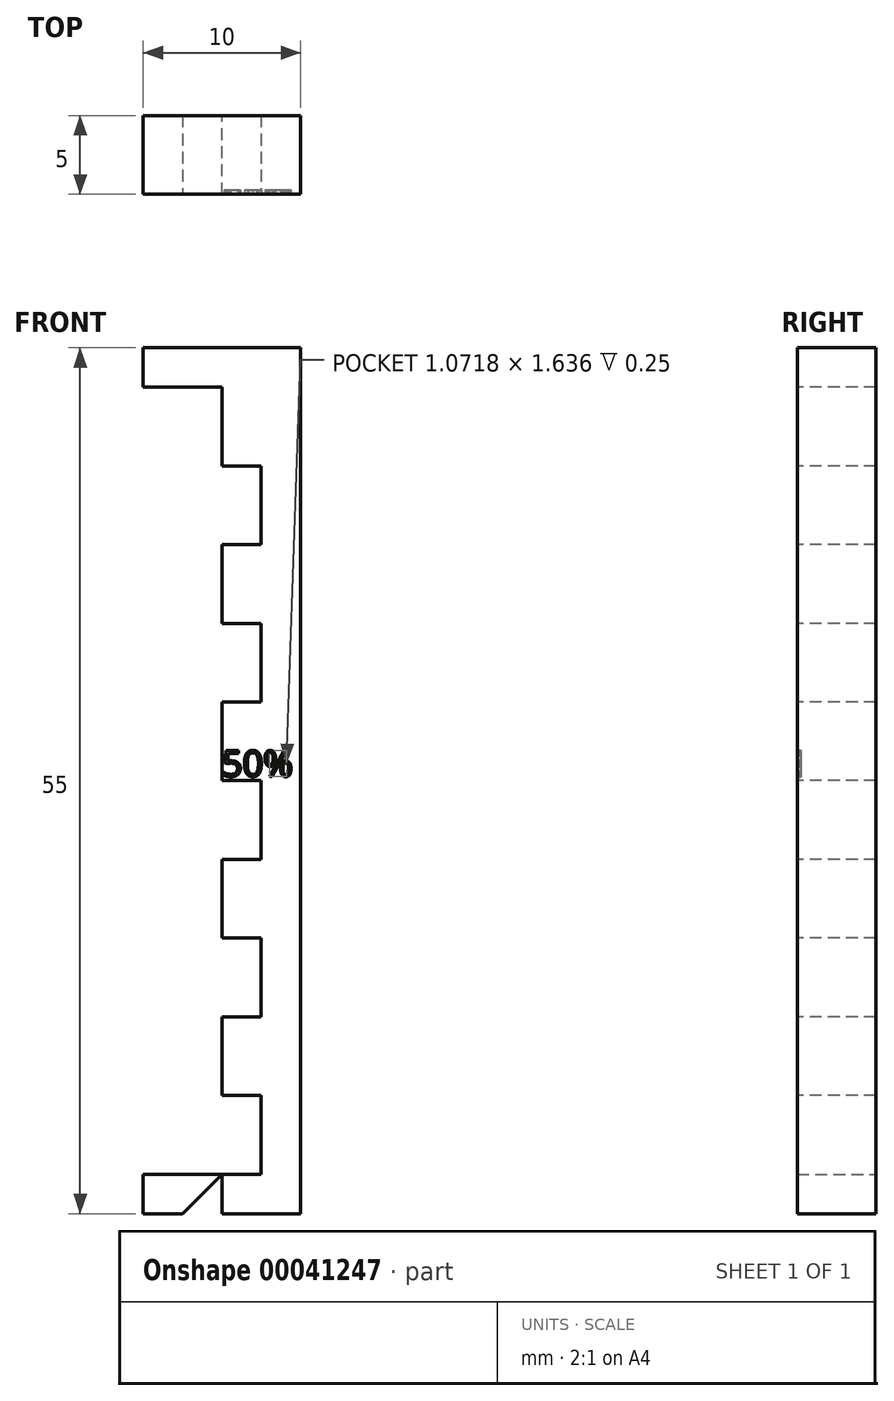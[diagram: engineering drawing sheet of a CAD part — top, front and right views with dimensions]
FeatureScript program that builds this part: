
annotation { "Feature Type Name" : "Feature", "Feature Type Description" : "" }
export const myFeature = defineFeature(function(context is Context, id is Id, definition is map)
    precondition{}
    {
        {
            var Q0;
            Q0=qCreatedBy(makeId("Front.planeOp"),FACE);
            var sketch = newSketch(context, id + "F0", { "sketchPlane" : qUnion([Q0])});
            skLineSegment(sketch, "E0.bottom", {"start": v(0, 10) * mm, "end": v(10, 10) * mm});
            skLineSegment(sketch, "E0.top", {"start": v(-10, -10) * mm, "end": v(10, -10) * mm});
            skLineSegment(sketch, "E0.left", {"start": v(-10, 0) * mm, "end": v(-10, -10) * mm});
            skLineSegment(sketch, "E0.right", {"start": v(10, 10) * mm, "end": v(10, -10) * mm});
            skLineSegment(sketch, "E1.top", {"start": v(-10, 0) * mm, "end": v(0, 0) * mm});
            skLineSegment(sketch, "E1.right", {"start": v(0, 10) * mm, "end": v(0, 0) * mm});
            skSolve(sketch);
        }
        {
            var Q0;
            Q0=makeQuery(id+"F0.imprint","IMPRINT",FACE,{"disambiguationData":[TD([[makeQuery(id+"F0.imprint","IMPRINT",EDGE,{"derivedFrom":sQuery(id+"F0.wireOp",EDGE,"E0.bottom")}),-1.0]])]});
            extrude(context, id + "F1", {"entities" : qUnion([Q0]), "oppositeDirection" : true, "depth" : 110 * mm});
        }
        {
            var Q0;
            Q0=makeQuery(id+"F1.opExtrude","CAP_FACE",FACE,{"disambiguationData":[OSD([sQuery(id+"F0.wireOp",EDGE,"E0.bottom"),sQuery(id+"F0.wireOp",EDGE,"E0.top"),sQuery(id+"F0.wireOp",EDGE,"E0.left"),sQuery(id+"F0.wireOp",EDGE,"E0.right"),sQuery(id+"F0.wireOp",EDGE,"E1.top"),sQuery(id+"F0.wireOp",EDGE,"E1.right")])],"isStart":true});
            var sketch = newSketch(context, id + "F2", { "sketchPlane" : qUnion([Q0])});
            skLineSegment(sketch, "E2.bottom", {"start": v(0, 10) * mm, "end": v(-10, 10) * mm});
            skLineSegment(sketch, "E2.top", {"start": v(0, 0) * mm, "end": v(-10, 0) * mm});
            skLineSegment(sketch, "E2.left", {"start": v(0, 10) * mm, "end": v(0, 0) * mm});
            skLineSegment(sketch, "E2.right", {"start": v(-10, 10) * mm, "end": v(-10, 0) * mm});
            skSolve(sketch);
        }
        {
            var Q0;
            Q0 = qSketchRegion(id + "F2", true);
            extrude(context, id + "F3", {"entities" : qUnion([Q0]), "oppositeDirection" : true, "depth" : 5 * mm});
        }
        {
            var Q0;
            Q0=makeQuery(id+"F3.opExtrude","CAP_EDGE",EDGE,{"disambiguationData":[OSD([sQuery(id+"F2.wireOp",EDGE,"E2.left")])],"isStart":true});
            chamfer(context, id + "F4", {"entities" : qUnion([Q0]), "width" : 5 * mm, "tangentPropagation" : true});
        }
        {
            var Q0;
            Q0=makeQuery(id+"F1.opExtrude","SWEPT_FACE",FACE,{"disambiguationData":[OSD([sQuery(id+"F0.wireOp",EDGE,"E0.bottom")])]});
            var sketch = newSketch(context, id + "F5", { "sketchPlane" : qUnion([Q0])});
            skLineSegment(sketch, "E3.bottom", {"start": v(-10, 115) * mm, "end": v(5, 115) * mm});
            skLineSegment(sketch, "E3.top", {"start": v(-10, 5) * mm, "end": v(5, 5) * mm});
            skLineSegment(sketch, "E3.left", {"start": v(-10, 115) * mm, "end": v(-10, 5) * mm});
            skLineSegment(sketch, "E3.right", {"start": v(5, 115) * mm, "end": v(5, 105) * mm});
            skLineSegment(sketch, "E4.top", {"start": v(0, 15) * mm, "end": v(5, 15) * mm});
            skLineSegment(sketch, "E4.left", {"start": v(0, 85) * mm, "end": v(0, 75) * mm});
            skLineSegment(sketch, "E5.bottom", {"start": v(0, 75) * mm, "end": v(5, 75) * mm});
            skLineSegment(sketch, "E5.top", {"start": v(0, 65) * mm, "end": v(5, 65) * mm});
            skLineSegment(sketch, "E6.bottom", {"start": v(0, 55) * mm, "end": v(5, 55) * mm});
            skLineSegment(sketch, "E6.top", {"start": v(0, 45) * mm, "end": v(5, 45) * mm});
            skLineSegment(sketch, "E7.bottom", {"start": v(0, 35) * mm, "end": v(5, 35) * mm});
            skLineSegment(sketch, "E7.top", {"start": v(0, 25) * mm, "end": v(5, 25) * mm});
            skLineSegment(sketch, "E8.trimOffspring", {"start": v(5, 15) * mm, "end": v(5, 5) * mm});
            skLineSegment(sketch, "E9.trimOffspring", {"start": v(0, 25) * mm, "end": v(0, 15) * mm});
            skLineSegment(sketch, "E10.trimOffspring", {"start": v(5, 35) * mm, "end": v(5, 25) * mm});
            skLineSegment(sketch, "E11.trimOffspring", {"start": v(0, 45) * mm, "end": v(0, 35) * mm});
            skLineSegment(sketch, "E12.trimOffspring", {"start": v(5, 55) * mm, "end": v(5, 45) * mm});
            skLineSegment(sketch, "E13.trimOffspring", {"start": v(5, 75) * mm, "end": v(5, 65) * mm});
            skLineSegment(sketch, "E14.trimOffspring", {"start": v(0, 65) * mm, "end": v(0, 55) * mm});
            skLineSegment(sketch, "E15", {"start": v(0, 85) * mm, "end": v(5, 85) * mm});
            skPoint(sketch, "E16.firstSnap0", {"position": v(5, 105) * mm});
            skLineSegment(sketch, "E16.bottom", {"start": v(0, 105) * mm, "end": v(5, 105) * mm});
            skLineSegment(sketch, "E16.top", {"start": v(0, 95) * mm, "end": v(5, 95) * mm});
            skLineSegment(sketch, "E16.left", {"start": v(0, 105) * mm, "end": v(0, 95) * mm});
            skLineSegment(sketch, "E17.trimOffspring", {"start": v(5, 95) * mm, "end": v(5, 85) * mm});
            skSolve(sketch);
        }
        {
            var Q0;
            Q0 = qSketchRegion(id + "F5", true);
            extrude(context, id + "F6", {"entities" : qUnion([Q0]), "operationType" : NewBodyOperationType.REMOVE, "oppositeDirection" : true, "depth" : 10 * mm});
        }
        {
            var Q0;
            Q0=makeQuery(id+"F1.opExtrude","SWEPT_FACE",FACE,{"disambiguationData":[OSD([sQuery(id+"F0.wireOp",EDGE,"E1.top")])]});
            var sketch = newSketch(context, id + "F7", { "sketchPlane" : qUnion([Q0])});
            skLineSegment(sketch, "E18.bottom", {"start": v(-10, 110) * mm, "end": v(5, 110) * mm});
            skLineSegment(sketch, "E18.top", {"start": v(-10, 105) * mm, "end": v(5, 105) * mm});
            skLineSegment(sketch, "E18.left", {"start": v(-10, 110) * mm, "end": v(-10, 105) * mm});
            skLineSegment(sketch, "E18.right", {"start": v(5, 110) * mm, "end": v(5, 105) * mm});
            skSolve(sketch);
        }
        {
            var Q0;
            Q0 = qSketchRegion(id + "F7", true);
            extrude(context, id + "F8", {"entities" : qUnion([Q0]), "operationType" : NewBodyOperationType.ADD, "depth" : 10 * mm});
        }
        {
            var Q0;
            Q0=makeQuery(id+"F8.boolean.opBoolean","MERGE",FACE,{"derivedFrom":[makeQuery(id+"F1.opExtrude","SWEPT_FACE",FACE,{"disambiguationData":[OSD([sQuery(id+"F0.wireOp",EDGE,"E0.bottom")])]}),makeQuery(id+"F8.opExtrude","CAP_FACE",FACE,{"disambiguationData":[OSD([sQuery(id+"F7.wireOp",EDGE,"E18.bottom"),sQuery(id+"F7.wireOp",EDGE,"E18.top"),sQuery(id+"F7.wireOp",EDGE,"E18.left"),sQuery(id+"F7.wireOp",EDGE,"E18.right")])],"isStart":false})]});
            var sketch = newSketch(context, id + "F9", { "sketchPlane" : qUnion([Q0])});
            skText(sketch, "E19", { "text": "50%", "fontName": "OpenSans-Regular.ttf"});
            const initialGuessF9  = {"E19": [0, 0.05554, 1, 0, 0.0033]};
            skSetInitialGuess(sketch, initialGuessF9);
            skSolve(sketch);
        }
        {
            var Q0;
            Q0 = qSketchRegion(id + "F9", true);
            extrude(context, id + "F10", {"entities" : qUnion([Q0]), "operationType" : NewBodyOperationType.REMOVE, "oppositeDirection" : true, "depth" : 0.5 * mm});
        }
        {
            var Q0;
            Q0=makeQuery(id+"F1.opExtrude","SWEPT_BODY",BODY,{"disambiguationData":[OSD([sQuery(id+"F0.wireOp",EDGE,"E0.bottom"),sQuery(id+"F0.wireOp",EDGE,"E0.top"),sQuery(id+"F0.wireOp",EDGE,"E0.left"),sQuery(id+"F0.wireOp",EDGE,"E0.right"),sQuery(id+"F0.wireOp",EDGE,"E1.top"),sQuery(id+"F0.wireOp",EDGE,"E1.right")])]});
            var Q1;
            Q1=makeQuery(id+"F3.opExtrude","SWEPT_BODY",BODY,{"disambiguationData":[OSD([sQuery(id+"F2.wireOp",EDGE,"E2.bottom"),sQuery(id+"F2.wireOp",EDGE,"E2.top"),sQuery(id+"F2.wireOp",EDGE,"E2.left"),sQuery(id+"F2.wireOp",EDGE,"E2.right")])]});
            var Q2;
            Q2=qCreatedBy(makeId("Origin.pointOp"),VERTEX);
            transform(context, id + "F11", {"entities" : qUnion([Q0, Q1]), "transformType" : TransformType.SCALE_UNIFORMLY, "scale" : 0.5, "makeCopy" : false, "scalePoint" : qUnion([Q2])});
        }
        {
            var Q0;
            Q0=makeQuery(id+"F1.opExtrude","SWEPT_BODY",BODY,{"disambiguationData":[OSD([sQuery(id+"F0.wireOp",EDGE,"E0.bottom"),sQuery(id+"F0.wireOp",EDGE,"E0.top"),sQuery(id+"F0.wireOp",EDGE,"E0.left"),sQuery(id+"F0.wireOp",EDGE,"E0.right"),sQuery(id+"F0.wireOp",EDGE,"E1.top"),sQuery(id+"F0.wireOp",EDGE,"E1.right")])]});
            var Q1;
            Q1=makeQuery(id+"F3.opExtrude","SWEPT_BODY",BODY,{"disambiguationData":[OSD([sQuery(id+"F2.wireOp",EDGE,"E2.bottom"),sQuery(id+"F2.wireOp",EDGE,"E2.top"),sQuery(id+"F2.wireOp",EDGE,"E2.left"),sQuery(id+"F2.wireOp",EDGE,"E2.right")])]});
            var Q2;
            Q2=makeQuery(id+"F1.opExtrude","CAP_EDGE",EDGE,{"disambiguationData":[OSD([sQuery(id+"F0.wireOp",EDGE,"E1.top")])],"isStart":true});
            transform(context, id + "F12", {"entities" : qUnion([Q0, Q1]), "transformType" : TransformType.ROTATION, "transformAxis" : qUnion([Q2]), "angle" : 90 * degree, "makeCopy" : false});
        }
        {
            var Q0;
            Q0=makeQuery(id+"F1.opExtrude","SWEPT_FACE",FACE,{"disambiguationData":[OSD([sQuery(id+"F0.wireOp",EDGE,"E0.top")])]});
            var Q1;
            Q1=makeQuery(id+"F1.opExtrude","SWEPT_FACE",FACE,{"disambiguationData":[OSD([sQuery(id+"F0.wireOp",EDGE,"E1.top")])]});
            extrude(context, id + "F13", {"entities" : qUnion([Q0]), "operationType" : NewBodyOperationType.REMOVE, "endBound" : BoundingType.UP_TO_SURFACE, "oppositeDirection" : true, "endBoundEntityFace" : qUnion([Q1]), "depth" : 1 * mm});
        }
    });
